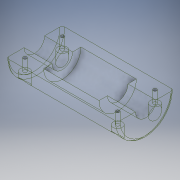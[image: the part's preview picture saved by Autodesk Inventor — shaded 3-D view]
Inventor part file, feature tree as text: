
AUTODESK INVENTOR PART (.ipt)
format: ipt  version: 2018 (Build 220112000, 112)  size: 200,704 bytes
history: native  units: in
note: dims shown in document units (in); Inventor stores cm internally (conversion verified against a paired STEP export)
features: extrude x5, sketch x5, plane x1, fillet x1
ambient origin geometry x8: Origin, YZ Plane, XZ Plane, XY Plane, X Axis, Y Axis, Z Axis, Center Point
bodies: Solid1 (feature_tree)
feature tree (12):
  extrude  "Extrusion1"  Depth=1.0in TaperAngle=0.0deg
  extrude  "Extrusion2"  Depth=1.5in TaperAngle=0.0deg
  extrude  "Extrusion3"  Depth=1.5in TaperAngle=0.0deg
  extrude  "Extrusion4"  Depth=0.5in
  plane  "Work Plane1"
  extrude  "Extrusion5"  Depth=1.5in
  fillet  "Fillet1"  Radius=0.5in
  sketch  "Sketch2"  dims[d0=1.0in d3=2.9685in d4=0.0in]
  sketch  "Sketch3"  dims[d5=0.55in d9=1.5in d10=0.0in]
  sketch  "Sketch4"  dims[d11=0.55in d17=1.5in d18=0.0in]
  sketch  "Sketch6"  dims[d45=0.5in d46=0.5in]
  sketch  "Sketch7"  dims[d47=0.5in d48=0.5in d49=0.5in d50=0.5in d51=0.5in d52=0.5in d53=0.19in d54=0.19in d55=0.19in d56=0.19in d57=1.5in d58=0.0in d59=-1.1196in d60=0.5in d61=0.5in d62=0.5in d63=0.5in d64=0.5in d65=0.5in d66=0.0in d67=0.0in d68=1.5in d69=1.5in d71=0.125in d74=0.55in d75=0.55in d77=0.95in d78=1.5in d79=1.5in d80=0.95in d81=0.5in]
